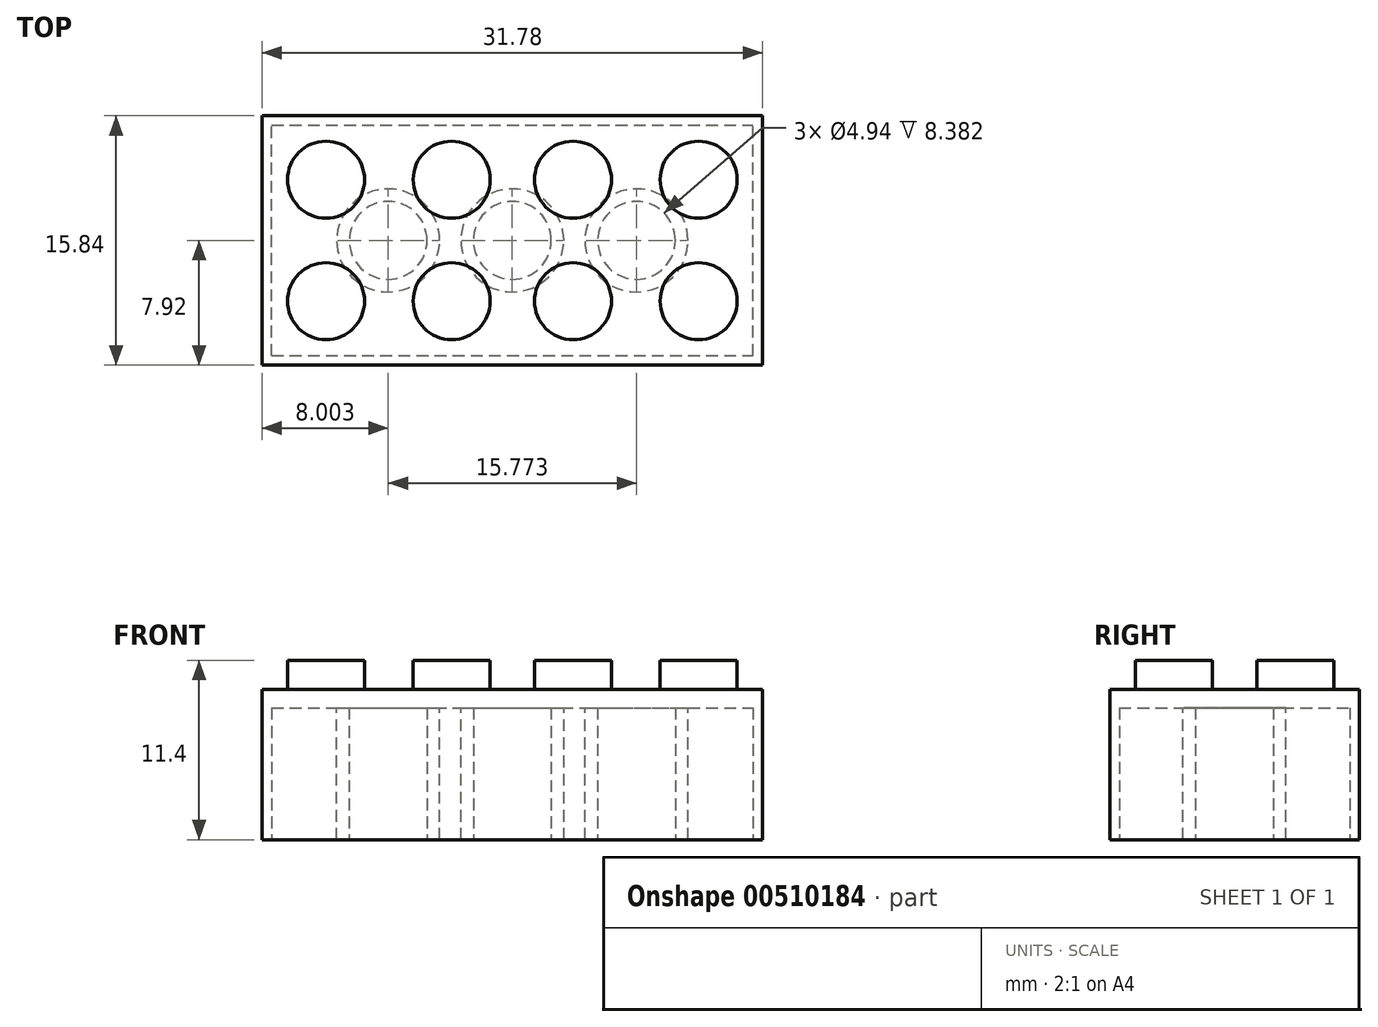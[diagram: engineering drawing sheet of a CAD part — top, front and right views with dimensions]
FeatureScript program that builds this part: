
annotation { "Feature Type Name" : "Feature", "Feature Type Description" : "" }
export const myFeature = defineFeature(function(context is Context, id is Id, definition is map)
    precondition{}
    {
        {
            var Q0;
            Q0=qCreatedBy(makeId("Top.planeOp"),FACE);
            var sketch = newSketch(context, id + "F0", { "sketchPlane" : qUnion([Q0])});
            skLineSegment(sketch, "E0.bottom", {"start": v(-15.89, 7.92) * mm, "end": v(15.89, 7.92) * mm});
            skLineSegment(sketch, "E0.top", {"start": v(-15.89, -7.92) * mm, "end": v(15.89, -7.92) * mm});
            skLineSegment(sketch, "E0.left", {"start": v(-15.89, 7.92) * mm, "end": v(-15.89, -7.92) * mm});
            skLineSegment(sketch, "E0.right", {"start": v(15.89, 7.92) * mm, "end": v(15.89, -7.92) * mm});
            skPoint(sketch, "E0.middle", {"position": v(0, 0) * mm});
            skSolve(sketch);
        }
        {
            var Q0;
            Q0 = qSketchRegion(id + "F0", true);
            extrude(context, id + "F1", {"entities" : qUnion([Q0]), "depth" : 9.54 * mm, "offsetDistance" : 25.4 * mm});
        }
        {
            var Q0;
            Q0=makeQuery(id+"F1.opExtrude","CAP_FACE",FACE,{"disambiguationData":[OSD([sQuery(id+"F0.wireOp",EDGE,"E0.bottom"),sQuery(id+"F0.wireOp",EDGE,"E0.top"),sQuery(id+"F0.wireOp",EDGE,"E0.left"),sQuery(id+"F0.wireOp",EDGE,"E0.right")])],"isStart":false});
            var sketch = newSketch(context, id + "F2", { "sketchPlane" : qUnion([Q0])});
            skCircle(sketch, "E1", {"center": v(-11.83, 3.86) * mm, "radius": 2.44 * mm});
            skCircle(sketch, "E2", {"center": v(-3.85, 3.86) * mm, "radius": 2.44 * mm});
            skCircle(sketch, "E3", {"center": v(3.85, 3.86) * mm, "radius": 2.44 * mm});
            skCircle(sketch, "E4", {"center": v(11.83, 3.86) * mm, "radius": 2.44 * mm});
            skCircle(sketch, "E5", {"center": v(11.83, -3.86) * mm, "radius": 2.44 * mm});
            skCircle(sketch, "E6", {"center": v(3.85, -3.86) * mm, "radius": 2.44 * mm});
            skCircle(sketch, "E7", {"center": v(-3.85, -3.86) * mm, "radius": 2.44 * mm});
            skCircle(sketch, "E8", {"center": v(-11.83, -3.86) * mm, "radius": 2.44 * mm});
            skSolve(sketch);
        }
        {
            var Q0;
            Q0=makeQuery(id+"F2.imprint","IMPRINT",FACE,{"disambiguationData":[TD([[makeQuery(id+"F2.imprint","IMPRINT",EDGE,{"derivedFrom":sQuery(id+"F2.wireOp",EDGE,"E1")}),1.0]])]});
            var Q1;
            Q1=makeQuery(id+"F2.imprint","IMPRINT",FACE,{"disambiguationData":[TD([[makeQuery(id+"F2.imprint","IMPRINT",EDGE,{"derivedFrom":sQuery(id+"F2.wireOp",EDGE,"E2")}),1.0]])]});
            var Q2;
            Q2=makeQuery(id+"F2.imprint","IMPRINT",FACE,{"disambiguationData":[TD([[makeQuery(id+"F2.imprint","IMPRINT",EDGE,{"derivedFrom":sQuery(id+"F2.wireOp",EDGE,"E3")}),1.0]])]});
            var Q3;
            Q3=makeQuery(id+"F2.imprint","IMPRINT",FACE,{"disambiguationData":[TD([[makeQuery(id+"F2.imprint","IMPRINT",EDGE,{"derivedFrom":sQuery(id+"F2.wireOp",EDGE,"E4")}),1.0]])]});
            var Q4;
            Q4=makeQuery(id+"F2.imprint","IMPRINT",FACE,{"disambiguationData":[TD([[makeQuery(id+"F2.imprint","IMPRINT",EDGE,{"derivedFrom":sQuery(id+"F2.wireOp",EDGE,"E8")}),1.0]])]});
            var Q5;
            Q5=makeQuery(id+"F2.imprint","IMPRINT",FACE,{"disambiguationData":[TD([[makeQuery(id+"F2.imprint","IMPRINT",EDGE,{"derivedFrom":sQuery(id+"F2.wireOp",EDGE,"E7")}),1.0]])]});
            var Q6;
            Q6=makeQuery(id+"F2.imprint","IMPRINT",FACE,{"disambiguationData":[TD([[makeQuery(id+"F2.imprint","IMPRINT",EDGE,{"derivedFrom":sQuery(id+"F2.wireOp",EDGE,"E6")}),1.0]])]});
            var Q7;
            Q7=makeQuery(id+"F2.imprint","IMPRINT",FACE,{"disambiguationData":[TD([[makeQuery(id+"F2.imprint","IMPRINT",EDGE,{"derivedFrom":sQuery(id+"F2.wireOp",EDGE,"E5")}),1.0]])]});
            extrude(context, id + "F3", {"entities" : qUnion([Q0, Q1, Q2, Q3, Q4, Q5, Q6, Q7]), "operationType" : NewBodyOperationType.ADD, "depth" : 1.87 * mm, "offsetDistance" : 25.4 * mm});
        }
        {
            var Q0;
            Q0=makeQuery(id+"F1.opExtrude","CAP_FACE",FACE,{"disambiguationData":[OSD([sQuery(id+"F0.wireOp",EDGE,"E0.bottom"),sQuery(id+"F0.wireOp",EDGE,"E0.top"),sQuery(id+"F0.wireOp",EDGE,"E0.left"),sQuery(id+"F0.wireOp",EDGE,"E0.right")])],"isStart":true});
            var Q1;
            Q1=qCreatedBy(makeId("Origin.pointOp"),VERTEX);
            cPlane(context, id + "F4", {"entities" : qUnion([Q0, Q1]), "cplaneType" : CPlaneType.PLANE_POINT, "offset" : 25.4 * mm, "width" : 152.4 * mm, "height" : 152.4 * mm});
        }
        {
            var Q0;
            Q0=qCreatedBy(id+"F4.planeOp",FACE);
            var sketch = newSketch(context, id + "F5", { "sketchPlane" : qUnion([Q0])});
            skLineSegment(sketch, "E9.bottom", {"start": v(-15.28, 7.32) * mm, "end": v(15.28, 7.32) * mm});
            skLineSegment(sketch, "E9.top", {"start": v(-15.28, -7.32) * mm, "end": v(15.28, -7.32) * mm});
            skLineSegment(sketch, "E9.left", {"start": v(-15.28, 7.32) * mm, "end": v(-15.28, -7.32) * mm});
            skLineSegment(sketch, "E9.right", {"start": v(15.28, 7.32) * mm, "end": v(15.28, -7.32) * mm});
            skPoint(sketch, "E9.middle", {"position": v(0, 0) * mm});
            skSolve(sketch);
        }
        {
            var Q0;
            Q0 = qSketchRegion(id + "F5", true);
            extrude(context, id + "F6", {"entities" : qUnion([Q0]), "operationType" : NewBodyOperationType.REMOVE, "oppositeDirection" : true, "depth" : 8.38 * mm, "offsetDistance" : 25.4 * mm});
        }
        {
            var Q0;
            Q0=makeQuery(id+"F6.boolean.opBoolean","COPY",FACE,{"derivedFrom":makeQuery(id+"F6.opExtrude","CAP_FACE",FACE,{"disambiguationData":[OSD([sQuery(id+"F5.wireOp",EDGE,"E9.bottom"),sQuery(id+"F5.wireOp",EDGE,"E9.top"),sQuery(id+"F5.wireOp",EDGE,"E9.left"),sQuery(id+"F5.wireOp",EDGE,"E9.right")])],"isStart":false})});
            var sketch = newSketch(context, id + "F7", { "sketchPlane" : qUnion([Q0])});
            skCircle(sketch, "E10", {"center": v(0, 0) * mm, "radius": 3.27 * mm});
            skCircle(sketch, "E11", {"center": v(-7.89, 0) * mm, "radius": 3.27 * mm});
            skCircle(sketch, "E12", {"center": v(7.89, 0) * mm, "radius": 3.27 * mm});
            skSolve(sketch);
        }
        {
            var Q0;
            Q0=makeQuery(id+"F7.imprint","IMPRINT",FACE,{"disambiguationData":[TD([[makeQuery(id+"F7.imprint","IMPRINT",EDGE,{"derivedFrom":sQuery(id+"F7.wireOp",EDGE,"E11")}),1.0]])]});
            var Q1;
            Q1=makeQuery(id+"F7.imprint","IMPRINT",FACE,{"disambiguationData":[TD([[makeQuery(id+"F7.imprint","IMPRINT",EDGE,{"derivedFrom":sQuery(id+"F7.wireOp",EDGE,"E10")}),1.0]])]});
            var Q2;
            Q2=makeQuery(id+"F7.imprint","IMPRINT",FACE,{"disambiguationData":[TD([[makeQuery(id+"F7.imprint","IMPRINT",EDGE,{"derivedFrom":sQuery(id+"F7.wireOp",EDGE,"E12")}),1.0]])]});
            extrude(context, id + "F8", {"entities" : qUnion([Q0, Q1, Q2]), "operationType" : NewBodyOperationType.ADD, "depth" : 8.38 * mm, "offsetDistance" : 25.4 * mm});
        }
        {
            var Q0;
            Q0=makeQuery(id+"F8.opExtrude","CAP_FACE",FACE,{"disambiguationData":[OSD([sQuery(id+"F7.wireOp",EDGE,"E10")])],"isStart":false});
            var sketch = newSketch(context, id + "F9", { "sketchPlane" : qUnion([Q0])});
            skCircle(sketch, "E13", {"center": v(-7.89, 0) * mm, "radius": 2.47 * mm});
            skCircle(sketch, "E14", {"center": v(0, 0) * mm, "radius": 2.47 * mm});
            skCircle(sketch, "E15", {"center": v(7.89, 0) * mm, "radius": 2.47 * mm});
            skSolve(sketch);
        }
        {
            var Q0;
            Q0=makeQuery(id+"F9.imprint","IMPRINT",FACE,{"disambiguationData":[TD([[makeQuery(id+"F9.imprint","IMPRINT",EDGE,{"derivedFrom":sQuery(id+"F9.wireOp",EDGE,"E13")}),1.0]])]});
            var Q1;
            Q1=makeQuery(id+"F9.imprint","IMPRINT",FACE,{"disambiguationData":[TD([[makeQuery(id+"F9.imprint","IMPRINT",EDGE,{"derivedFrom":sQuery(id+"F9.wireOp",EDGE,"E14")}),1.0]])]});
            var Q2;
            Q2=makeQuery(id+"F9.imprint","IMPRINT",FACE,{"disambiguationData":[TD([[makeQuery(id+"F9.imprint","IMPRINT",EDGE,{"derivedFrom":sQuery(id+"F9.wireOp",EDGE,"E15")}),1.0]])]});
            extrude(context, id + "F10", {"entities" : qUnion([Q0, Q1, Q2]), "operationType" : NewBodyOperationType.REMOVE, "oppositeDirection" : true, "depth" : 8.38 * mm, "offsetDistance" : 25.4 * mm});
        }
    });
